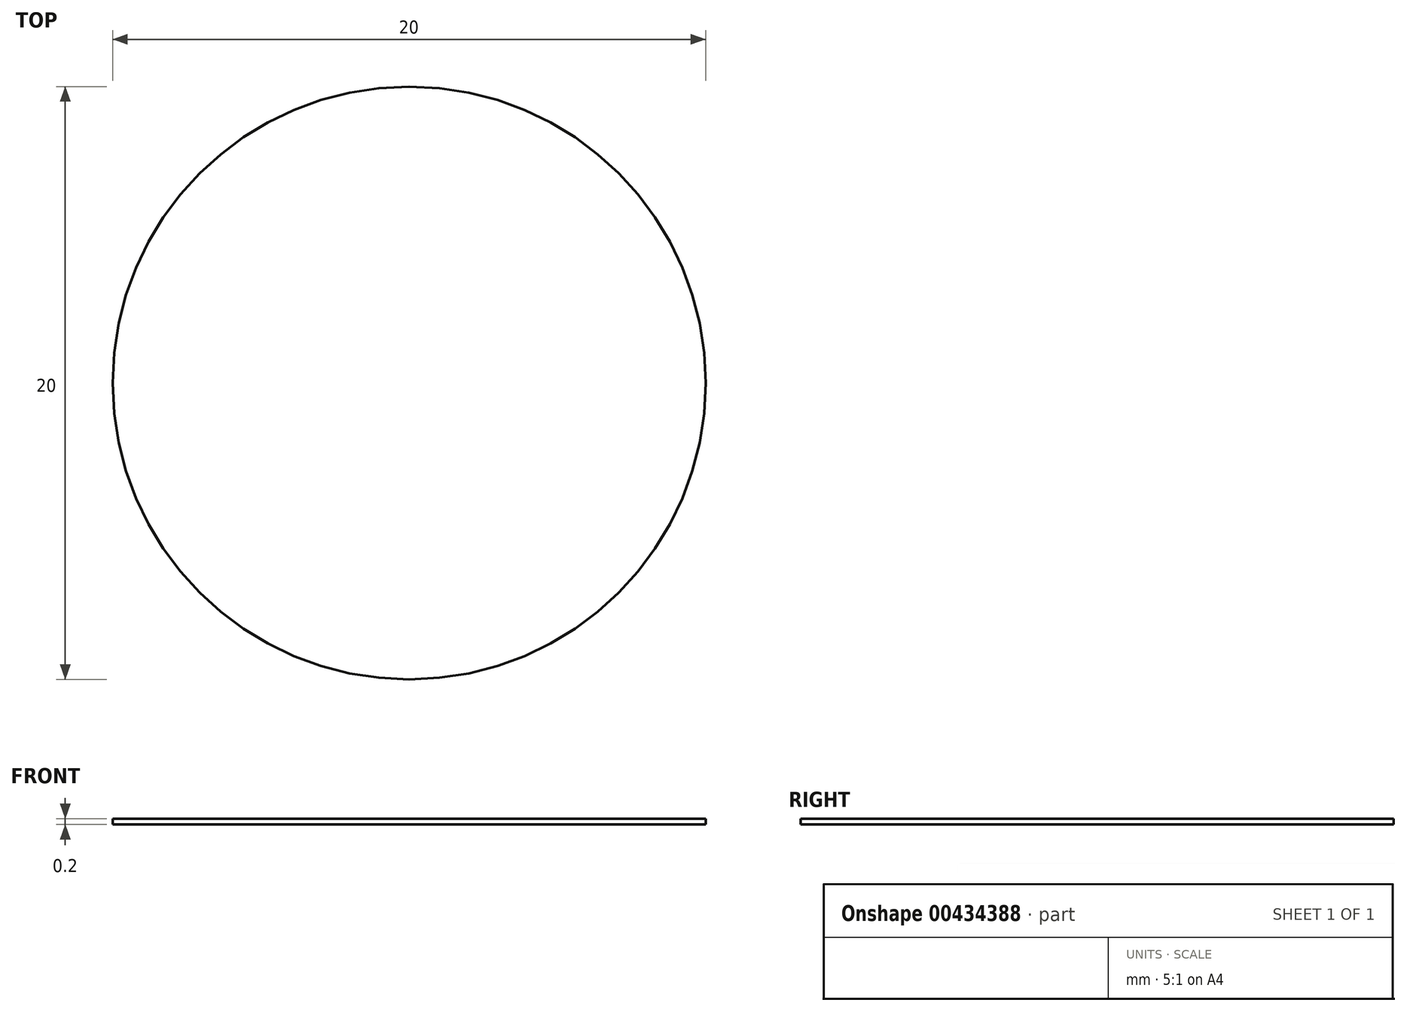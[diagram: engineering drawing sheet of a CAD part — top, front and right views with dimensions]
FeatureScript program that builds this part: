
annotation { "Feature Type Name" : "Feature", "Feature Type Description" : "" }
export const myFeature = defineFeature(function(context is Context, id is Id, definition is map)
    precondition{}
    {
        {
            var Q0;
            Q0=qCreatedBy(makeId("Top.planeOp"),FACE);
            var sketch = newSketch(context, id + "F0", { "sketchPlane" : qUnion([Q0])});
            skCircle(sketch, "E0", {"center": v(0, 0) * mm, "radius": 10 * mm});
            skSolve(sketch);
        }
        {
            var Q0;
            Q0 = qSketchRegion(id + "F0", true);
            extrude(context, id + "F1", {"entities" : qUnion([Q0]), "depth" : 0.2 * mm});
        }
    });
